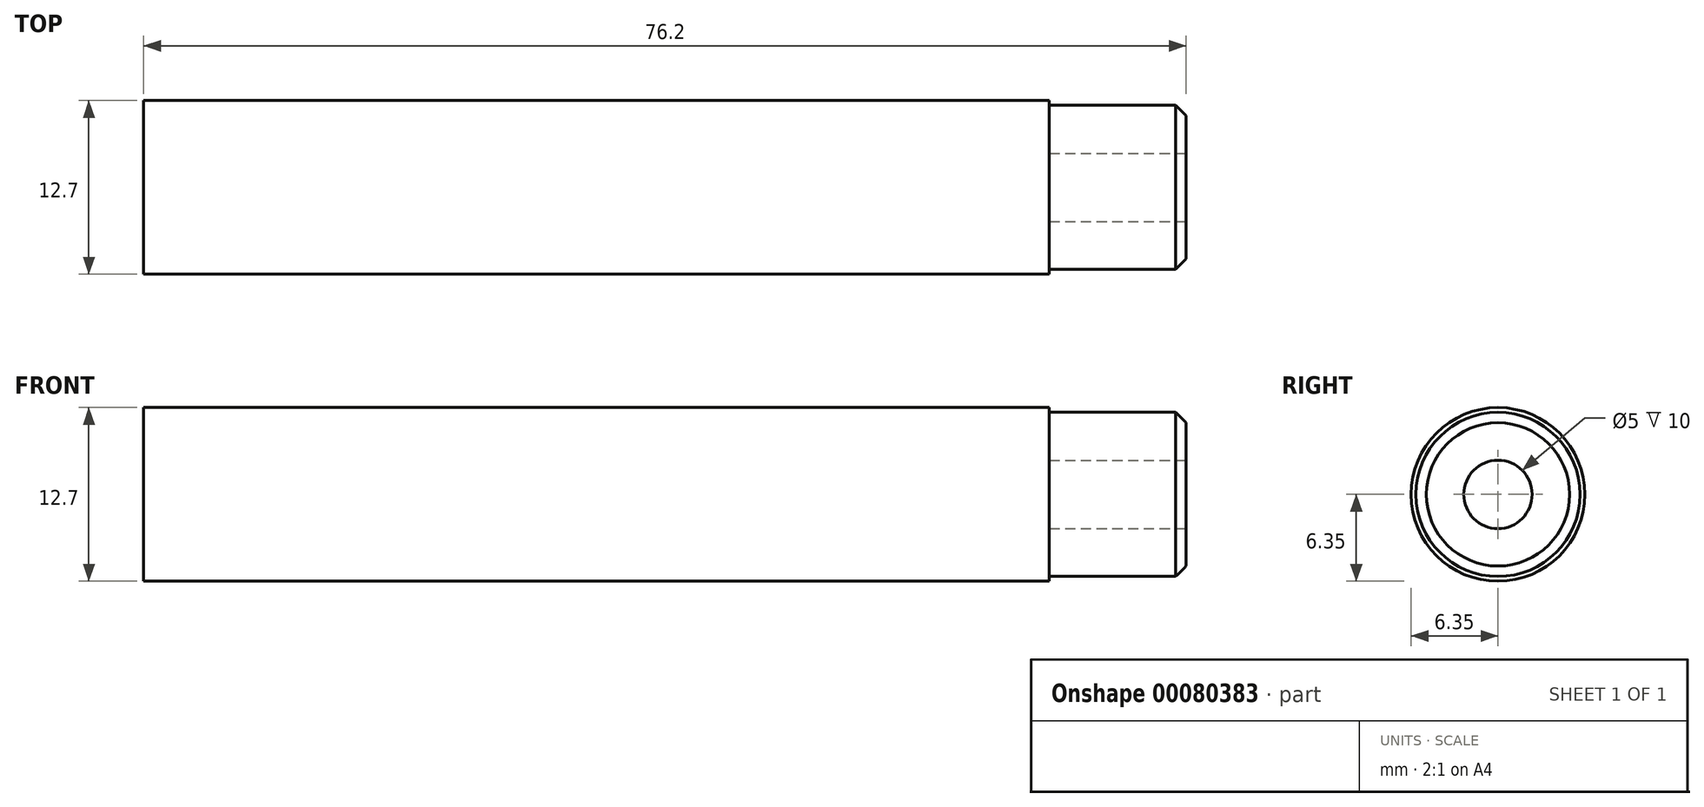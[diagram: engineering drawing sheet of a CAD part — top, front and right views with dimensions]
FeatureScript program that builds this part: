
annotation { "Feature Type Name" : "Feature", "Feature Type Description" : "" }
export const myFeature = defineFeature(function(context is Context, id is Id, definition is map)
    precondition{}
    {
        {
            var Q0;
            Q0=qCreatedBy(makeId("Right.planeOp"),FACE);
            var sketch = newSketch(context, id + "F0", { "sketchPlane" : qUnion([Q0])});
            skCircle(sketch, "E0", {"center": v(0, 0) * mm, "radius": 6 * mm});
            skSolve(sketch);
        }
        {
            var Q0;
            Q0 = qSketchRegion(id + "F0", true);
            extrude(context, id + "F1", {"entities" : qUnion([Q0]), "depth" : 76.2 * mm});
        }
        {
            var Q0;
            Q0=makeQuery(id+"F1.opExtrude","CAP_EDGE",EDGE,{"disambiguationData":[OSD([sQuery(id+"F0.wireOp",EDGE,"E0")])],"isStart":false});
            chamfer(context, id + "F2", {"entities" : qUnion([Q0]), "width" : 0.76 * mm, "tangentPropagation" : true});
        }
        {
            var Q0;
            Q0=makeQuery(id+"F1.opExtrude","CAP_FACE",FACE,{"disambiguationData":[OSD([sQuery(id+"F0.wireOp",EDGE,"E0")])],"isStart":false});
            var sketch = newSketch(context, id + "F3", { "sketchPlane" : qUnion([Q0])});
            skPoint(sketch, "E1", {"position": v(0, 0) * mm});
            skSolve(sketch);
        }
        {
            var Q0;
            Q0=sQuery(id+"F3.wireOp",VERTEX,"E1");
            var Q1;
            Q1=makeQuery(id+"F1.opExtrude","SWEPT_BODY",BODY,{"disambiguationData":[OSD([sQuery(id+"F0.wireOp",EDGE,"E0")])]});
            hole(context, id + "F4", {"style" : HoleStyle.SIMPLE, "endStyle" : HoleEndStyle.BLIND, "standardTappedOrClearance" : lookupTablePath({ "standard" : "ISO", "engagement" : "75%", "pitch" : "1 mm", "size" : "M6", "type" : "Tapped" }), "standardBlindInLast" : lookupTablePath({ "standard" : "ISO", "engagement" : "75%", "pitch" : "1 mm", "size" : "M6", "type" : "Tapped" }), "holeDiameter" : 5 * mm, "holeDepth" : 16 * mm, "locations" : qUnion([Q0]), "scope" : qUnion([Q1]), "majorDiameter" : 6 * mm});
        }
        {
            var Q0;
            Q0=makeQuery(id+"F1.opExtrude","CAP_FACE",FACE,{"disambiguationData":[OSD([sQuery(id+"F0.wireOp",EDGE,"E0")])],"isStart":false});
            cPlane(context, id + "F5", {"entities" : qUnion([Q0]), "cplaneType" : CPlaneType.OFFSET, "offset" : 10 * mm, "oppositeDirection" : true, "width" : 152.4 * mm, "height" : 152.4 * mm});
        }
        {
            var Q0;
            Q0=qCreatedBy(id+"F5.planeOp",FACE);
            var sketch = newSketch(context, id + "F6", { "sketchPlane" : qUnion([Q0])});
            skCircle(sketch, "E2", {"center": v(0, 0) * mm, "radius": 6.35 * mm});
            skSolve(sketch);
        }
        {
            var Q0;
            Q0 = qSketchRegion(id + "F6", true);
            var Q1;
            Q1=makeQuery(id+"F1.opExtrude","CAP_FACE",FACE,{"disambiguationData":[OSD([sQuery(id+"F0.wireOp",EDGE,"E0")])],"isStart":true});
            extrude(context, id + "F7", {"entities" : qUnion([Q0]), "operationType" : NewBodyOperationType.ADD, "endBound" : BoundingType.UP_TO_SURFACE, "oppositeDirection" : true, "endBoundEntityFace" : qUnion([Q1]), "depth" : 25.4 * mm});
        }
    });
